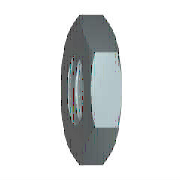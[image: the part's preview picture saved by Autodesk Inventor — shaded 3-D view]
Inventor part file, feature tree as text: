
AUTODESK INVENTOR PART (.ipt)
format: ipt  version: 2020 (Build 240168000, 168)  size: 167,936 bytes
history: native  units: mm (DEFAULTED — no unit token found)
features: sketch x3, chamfer x1, hole x1, other x1, plane x1
ambient origin geometry x7: Origin, YZ Plane, XZ Plane, X Axis, Y Axis, Z Axis, Center Point
bodies: Solid1 (feature_tree), Body (feature_tree)
feature tree (7):
  chamfer  "Chamfer1"  Angle=30.0deg  [1 undecoded]
  hole  "Thread"  [1 undecoded]
  other  "Work Axis1"
  plane  "Work Plane1"
  sketch  "Sketch1"  dims[d0=9.237604mm]
  sketch  "Sketch2"  dims[d1=2.7mm]
  sketch  "Sketch3"  dims[d2=0.0mm d3=30.0deg d4=30.0deg d5=6.9mm d6=6.9mm d7=90.0deg d25=4.134mm d26=6.0mm d27=4.0mm d28=2.0mm d29=14.3117mm d30=8.0mm d31=20.594885mm d8=0.433013mm d9=30.0deg d10=0.433013mm d11=30.0deg d13=0.0mm d14=0.0mm d39=0.0mm d40=0.433013mm d41=0.433013mm d42=0.0mm]
note: 2 required parameter values undecoded (feature->parameter linkage not recoverable at this tier; creation-order binding heuristic only, values carry confidence <= 0.55)
